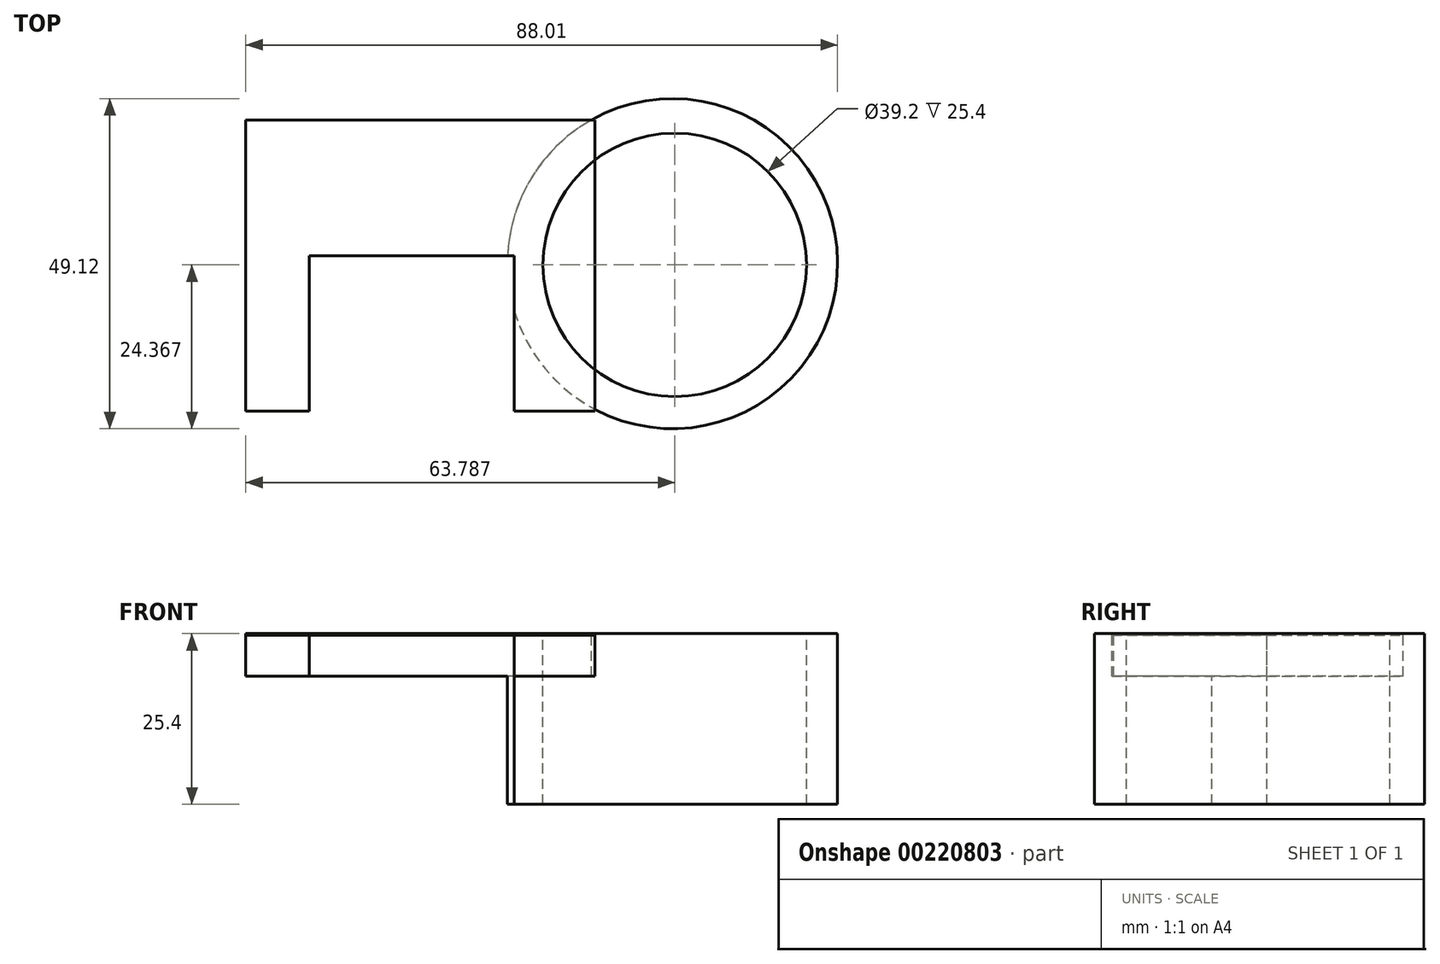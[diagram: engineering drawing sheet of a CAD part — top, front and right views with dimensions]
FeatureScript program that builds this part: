
annotation { "Feature Type Name" : "Feature", "Feature Type Description" : "" }
export const myFeature = defineFeature(function(context is Context, id is Id, definition is map)
    precondition{}
    {
        {
            var Q0;
            Q0=qCreatedBy(makeId("Top.planeOp"),FACE);
            var sketch = newSketch(context, id + "F0", { "sketchPlane" : qUnion([Q0])});
            skLineSegment(sketch, "E0.bottom", {"start": v(0, 7.84) * mm, "end": v(-51.91, 7.84) * mm});
            skLineSegment(sketch, "E0.top", {"start": v(0, 51.2) * mm, "end": v(-51.91, 51.2) * mm});
            skLineSegment(sketch, "E0.left", {"start": v(0, 7.84) * mm, "end": v(0, 51.2) * mm});
            skLineSegment(sketch, "E0.right", {"start": v(-51.91, 7.84) * mm, "end": v(-51.91, 51.2) * mm});
            skSolve(sketch);
        }
        {
            var Q0;
            Q0 = qSketchRegion(id + "F0", true);
            extrude(context, id + "F1", {"entities" : qUnion([Q0]), "oppositeDirection" : true, "depth" : 6.35 * mm});
        }
        {
            var Q0;
            Q0=qCreatedBy(makeId("Top.planeOp"),FACE);
            var sketch = newSketch(context, id + "F2", { "sketchPlane" : qUnion([Q0])});
            skCircle(sketch, "E1", {"center": v(11.54, 29.8) * mm, "radius": 24.56 * mm});
            skPoint(sketch, "E1.first.point", {"position": v(0, 51.49) * mm});
            skPoint(sketch, "E1.second.point", {"position": v(22.53, 7.84) * mm});
            skPoint(sketch, "E1.third.point", {"position": v(0, 8.13) * mm});
            skSolve(sketch);
        }
        {
            var Q0;
            Q0 = qSketchRegion(id + "F2", true);
            extrude(context, id + "F3", {"entities" : qUnion([Q0]), "operationType" : NewBodyOperationType.ADD, "oppositeDirection" : true, "depth" : 25.4 * mm});
        }
        {
            var Q0;
            Q0=qCreatedBy(makeId("Top.planeOp"),FACE);
            var sketch = newSketch(context, id + "F4", { "sketchPlane" : qUnion([Q0])});
            skCircle(sketch, "E2", {"center": v(11.88, 29.62) * mm, "radius": 19.6 * mm});
            skPoint(sketch, "E2.first.point", {"position": v(0, 45.21) * mm});
            skPoint(sketch, "E2.second.point", {"position": v(23.1, 13.55) * mm});
            skPoint(sketch, "E2.third.point", {"position": v(-6.56, 22.96) * mm});
            skSolve(sketch);
        }
        {
            var Q0;
            Q0 = qSketchRegion(id + "F4", true);
            extrude(context, id + "F5", {"entities" : qUnion([Q0]), "operationType" : NewBodyOperationType.REMOVE, "oppositeDirection" : true, "depth" : 43.18 * mm});
        }
        {
            var Q0;
            Q0 = qSketchRegion(id + "F0", true);
            extrude(context, id + "F6", {"entities" : qUnion([Q0]), "oppositeDirection" : true, "depth" : 0.25 * mm});
        }
        {
            var Q0;
            Q0=qCreatedBy(makeId("Top.planeOp"),FACE);
            var sketch = newSketch(context, id + "F7", { "sketchPlane" : qUnion([Q0])});
            skLineSegment(sketch, "E3.bottom", {"start": v(-42.5, 30.95) * mm, "end": v(-11.98, 30.95) * mm});
            skLineSegment(sketch, "E3.top", {"start": v(-42.5, 25.53) * mm, "end": v(-11.98, 25.53) * mm});
            skLineSegment(sketch, "E3.left", {"start": v(-42.5, 30.95) * mm, "end": v(-42.5, 25.53) * mm});
            skLineSegment(sketch, "E3.right", {"start": v(-11.98, 30.95) * mm, "end": v(-11.98, 25.53) * mm});
            skSolve(sketch);
        }
        {
            var Q0;
            Q0 = qSketchRegion(id + "F7", true);
            extrude(context, id + "F8", {"entities" : qUnion([Q0]), "oppositeDirection" : true, "depth" : 25.4 * mm});
        }
        {
            var Q0;
            Q0=makeQuery(id+"F8.opExtrude","SWEPT_FACE",FACE,{"disambiguationData":[OSD([sQuery(id+"F7.wireOp",EDGE,"E3.bottom")])]});
            var sketch = newSketch(context, id + "F9", { "sketchPlane" : qUnion([Q0])});
            skLineSegment(sketch, "E4.0", {"start": v(42.5, -25.4) * mm, "end": v(42.5, 0) * mm});
            skPoint(sketch, "E5.0", {"position": v(27.24, -25.4) * mm});
            skLineSegment(sketch, "E6.0", {"start": v(42.5, -25.4) * mm, "end": v(11.98, -25.4) * mm});
            skLineSegment(sketch, "E7", {"start": v(42.5, -7.56) * mm, "end": v(11.98, -25.4) * mm});
            skSolve(sketch);
        }
        {
            var Q0;
            Q0=makeQuery(id+"F8.opExtrude","SWEPT_FACE",FACE,{"disambiguationData":[OSD([sQuery(id+"F7.wireOp",EDGE,"E3.top")])]});
            var Q1;
            {var subQ3=sQuery(id+"F9.wireOp",EDGE,"E7");Q1=makeQuery(id+"F9.imprint","IMPRINT",FACE,{"disambiguationData":[TD([[makeQuery(id+"F9.imprint","IMPRINT",EDGE,{"derivedFrom":subQ3}),-1.0]])]});}
            var Q2;
            {var subQ0=sQuery(id+"F9.wireOp",EDGE,"E6.0");Q2=makeQuery(id+"F9.imprint","IMPRINT",FACE,{"disambiguationData":[TD([[makeQuery(id+"F9.imprint","IMPRINT",EDGE,{"derivedFrom":subQ0}),-1.0]])]});}
            extrude(context, id + "F10", {"entities" : qUnion([Q0, Q1, Q2]), "operationType" : NewBodyOperationType.REMOVE, "depth" : 46.74 * mm});
        }
    });
